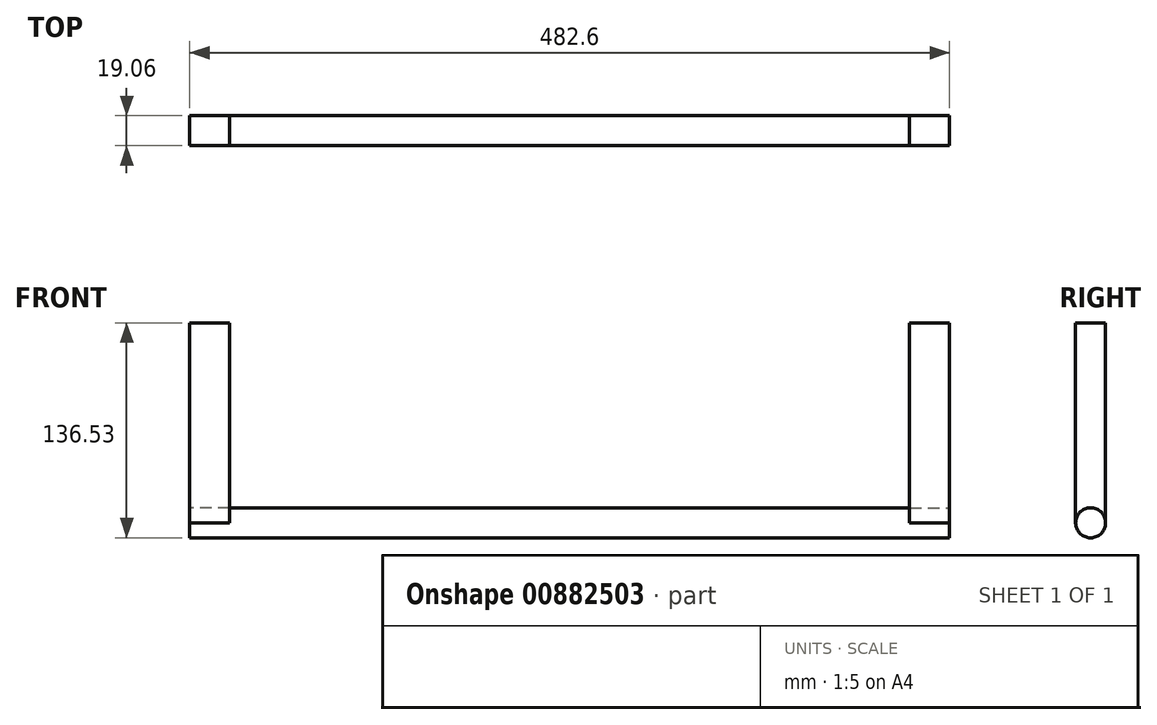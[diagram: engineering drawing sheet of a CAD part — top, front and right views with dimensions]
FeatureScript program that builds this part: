
annotation { "Feature Type Name" : "Feature", "Feature Type Description" : "" }
export const myFeature = defineFeature(function(context is Context, id is Id, definition is map)
    precondition{}
    {
        {
            var Q0;
            Q0=qCreatedBy(makeId("Right.planeOp"),FACE);
            var sketch = newSketch(context, id + "F0", { "sketchPlane" : qUnion([Q0])});
            skCircle(sketch, "E0", {"center": v(0, 0) * mm, "radius": 9.53 * mm});
            skSolve(sketch);
        }
        {
            var Q0;
            Q0=makeQuery(id+"F0.imprint","IMPRINT",FACE,{"disambiguationData":[TD([[makeQuery(id+"F0.imprint","IMPRINT",EDGE,{"derivedFrom":sQuery(id+"F0.wireOp",EDGE,"E0")}),1.0]])]});
            extrude(context, id + "F1", {"entities" : qUnion([Q0]), "depth" : 482.6 * mm, "offsetDistance" : 25.4 * mm});
        }
        {
            var Q0;
            Q0=makeQuery(id+"F1.opExtrude","CAP_FACE",FACE,{"disambiguationData":[OSD([sQuery(id+"F0.wireOp",EDGE,"E0")])],"isStart":false});
            var sketch = newSketch(context, id + "F2", { "sketchPlane" : qUnion([Q0])});
            skLineSegment(sketch, "E1", {"start": v(-9.53, 0) * mm, "end": v(-9.53, 127) * mm});
            skLineSegment(sketch, "E2", {"start": v(-9.53, 127) * mm, "end": v(9.53, 127) * mm});
            skLineSegment(sketch, "E3", {"start": v(9.52, 127) * mm, "end": v(9.53, 0) * mm});
            skSolve(sketch);
        }
        {
            var Q0;
            {var subQ0=sQuery(id+"F2.wireOp",EDGE,"E1");Q0=makeQuery(id+"F2.imprint","IMPRINT",FACE,{"disambiguationData":[TD([[makeQuery(id+"F2.imprint","IMPRINT",EDGE,{"derivedFrom":subQ0}),-1.0]])]});}
            extrude(context, id + "F3", {"entities" : qUnion([Q0]), "oppositeDirection" : true, "depth" : 25.4 * mm, "offsetDistance" : 25.4 * mm});
        }
        {
            var Q0;
            Q0=makeQuery(id+"F1.opExtrude","CAP_FACE",FACE,{"disambiguationData":[OSD([sQuery(id+"F0.wireOp",EDGE,"E0")])],"isStart":true});
            var sketch = newSketch(context, id + "F4", { "sketchPlane" : qUnion([Q0])});
            skLineSegment(sketch, "E4", {"start": v(-9.53, 0) * mm, "end": v(-9.53, 127) * mm});
            skLineSegment(sketch, "E5", {"start": v(-9.53, 127) * mm, "end": v(9.53, 127) * mm});
            skLineSegment(sketch, "E6", {"start": v(9.52, 127) * mm, "end": v(9.53, 0) * mm});
            skSolve(sketch);
        }
        {
            var Q0;
            {var subQ0=sQuery(id+"F4.wireOp",EDGE,"E4");Q0=makeQuery(id+"F4.imprint","IMPRINT",FACE,{"disambiguationData":[TD([[makeQuery(id+"F4.imprint","IMPRINT",EDGE,{"derivedFrom":subQ0}),-1.0]])]});}
            extrude(context, id + "F5", {"entities" : qUnion([Q0]), "oppositeDirection" : true, "depth" : 25.4 * mm, "offsetDistance" : 25.4 * mm});
        }
    });
